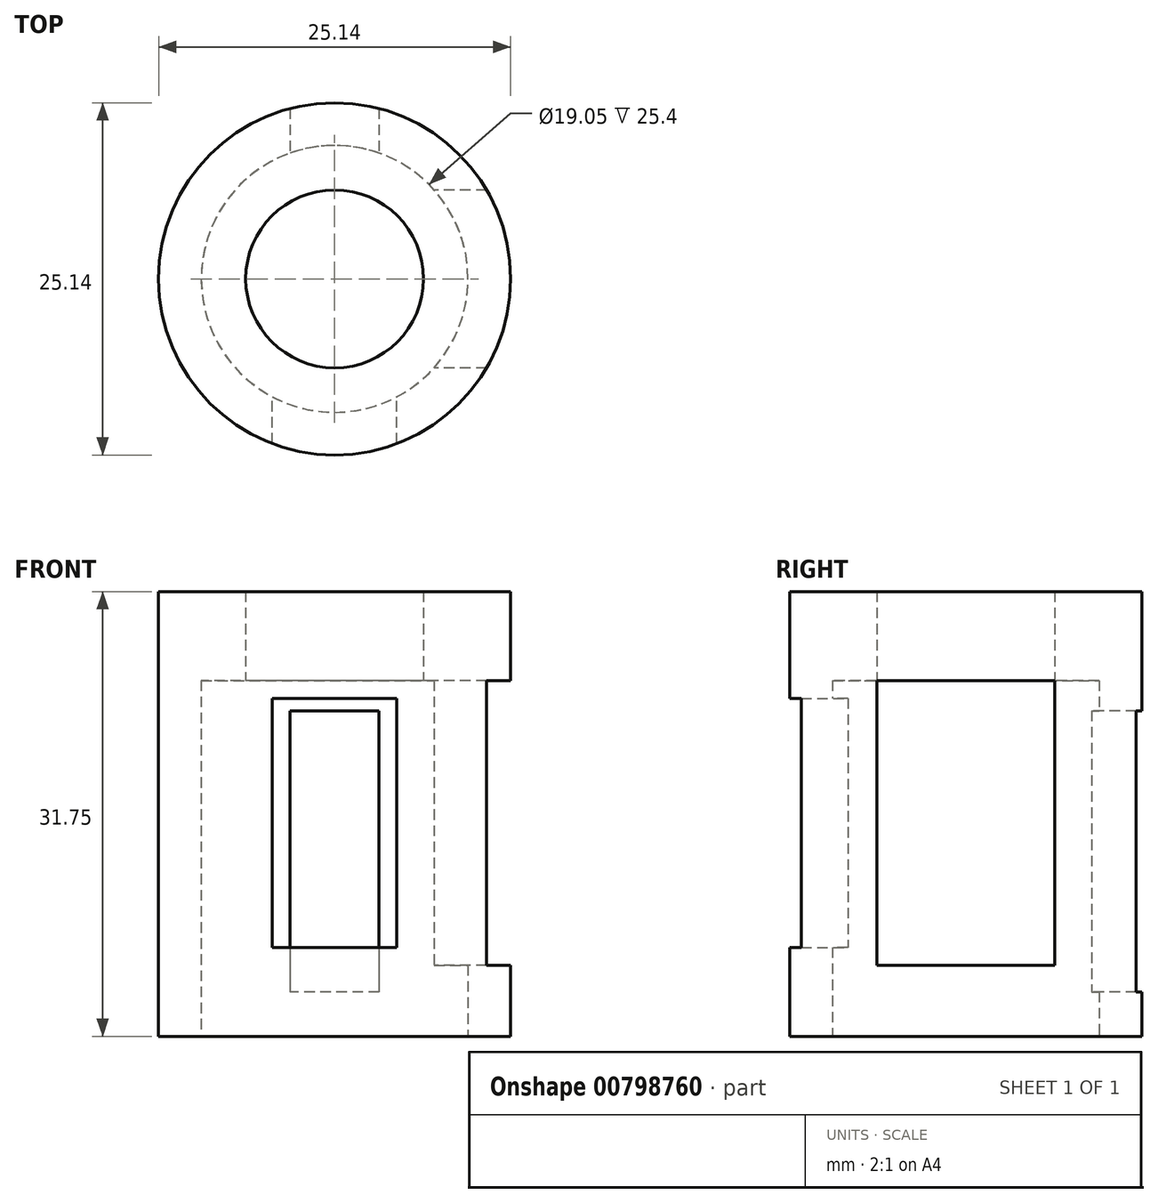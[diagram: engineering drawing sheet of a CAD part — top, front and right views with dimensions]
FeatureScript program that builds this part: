
annotation { "Feature Type Name" : "Feature", "Feature Type Description" : "" }
export const myFeature = defineFeature(function(context is Context, id is Id, definition is map)
    precondition{}
    {
        {
            var Q0;
            Q0=qCreatedBy(makeId("Top.planeOp"),FACE);
            var sketch = newSketch(context, id + "F0", { "sketchPlane" : qUnion([Q0])});
            skCircle(sketch, "E0", {"center": v(0, 0) * mm, "radius": 12.57 * mm});
            skSolve(sketch);
        }
        {
            var Q0;
            Q0=makeQuery(id+"F0.imprint","IMPRINT",FACE,{"disambiguationData":[TD([[makeQuery(id+"F0.imprint","IMPRINT",EDGE,{"derivedFrom":sQuery(id+"F0.wireOp",EDGE,"E0")}),1.0]])]});
            extrude(context, id + "F1", {"entities" : qUnion([Q0]), "depth" : 31.75 * mm, "offsetDistance" : 25.4 * mm});
        }
        {
            var Q0;
            Q0=qCreatedBy(makeId("Right.planeOp"),FACE);
            cPlane(context, id + "F2", {"entities" : qUnion([Q0]), "cplaneType" : CPlaneType.OFFSET, "offset" : 5.6 * mm, "width" : 152.4 * mm, "height" : 152.4 * mm});
        }
        {
            var Q0;
            Q0=qCreatedBy(id+"F2.planeOp",FACE);
            var sketch = newSketch(context, id + "F3", { "sketchPlane" : qUnion([Q0])});
            skLineSegment(sketch, "E1.bottom", {"start": v(-6.35, 25.4) * mm, "end": v(6.35, 25.4) * mm});
            skLineSegment(sketch, "E1.top", {"start": v(-6.35, 5.08) * mm, "end": v(6.35, 5.08) * mm});
            skLineSegment(sketch, "E1.left", {"start": v(-6.35, 25.4) * mm, "end": v(-6.35, 5.08) * mm});
            skLineSegment(sketch, "E1.right", {"start": v(6.35, 25.4) * mm, "end": v(6.35, 5.08) * mm});
            skSolve(sketch);
        }
        {
            var Q0;
            Q0 = qSketchRegion(id + "F3", true);
            extrude(context, id + "F4", {"entities" : qUnion([Q0]), "operationType" : NewBodyOperationType.REMOVE, "endBound" : BoundingType.THROUGH_ALL, "depth" : 25.4 * mm, "offsetDistance" : 25.4 * mm});
        }
        {
            var Q0;
            Q0=qCreatedBy(makeId("Front.planeOp"),FACE);
            cPlane(context, id + "F5", {"entities" : qUnion([Q0]), "cplaneType" : CPlaneType.OFFSET, "offset" : 2.41 * mm, "oppositeDirection" : true, "width" : 152.4 * mm, "height" : 152.4 * mm});
        }
        {
            var Q0;
            Q0=qCreatedBy(id+"F5.planeOp",FACE);
            var sketch = newSketch(context, id + "F6", { "sketchPlane" : qUnion([Q0])});
            skLineSegment(sketch, "E2.bottom", {"start": v(3.18, 23.24) * mm, "end": v(-3.18, 23.24) * mm});
            skLineSegment(sketch, "E2.top", {"start": v(3.17, 3.18) * mm, "end": v(-3.17, 3.18) * mm});
            skLineSegment(sketch, "E2.left", {"start": v(3.17, 23.24) * mm, "end": v(3.17, 3.18) * mm});
            skLineSegment(sketch, "E2.right", {"start": v(-3.18, 23.24) * mm, "end": v(-3.18, 3.18) * mm});
            skSolve(sketch);
        }
        {
            var Q0;
            Q0 = qSketchRegion(id + "F6", true);
            extrude(context, id + "F7", {"entities" : qUnion([Q0]), "operationType" : NewBodyOperationType.REMOVE, "endBound" : BoundingType.THROUGH_ALL, "oppositeDirection" : true, "depth" : 25.4 * mm, "offsetDistance" : 25.4 * mm});
        }
        {
            var Q0;
            Q0=qCreatedBy(makeId("Front.planeOp"),FACE);
            var sketch = newSketch(context, id + "F8", { "sketchPlane" : qUnion([Q0])});
            skLineSegment(sketch, "E3.bottom", {"start": v(-4.44, 24.13) * mm, "end": v(4.44, 24.13) * mm});
            skLineSegment(sketch, "E3.top", {"start": v(-4.44, 6.35) * mm, "end": v(4.44, 6.35) * mm});
            skLineSegment(sketch, "E3.left", {"start": v(-4.45, 24.13) * mm, "end": v(-4.45, 6.35) * mm});
            skLineSegment(sketch, "E3.right", {"start": v(4.45, 24.13) * mm, "end": v(4.45, 6.35) * mm});
            skSolve(sketch);
        }
        {
            var Q0;
            Q0 = qSketchRegion(id + "F8", true);
            extrude(context, id + "F9", {"entities" : qUnion([Q0]), "operationType" : NewBodyOperationType.REMOVE, "endBound" : BoundingType.THROUGH_ALL, "depth" : 25.4 * mm, "offsetDistance" : 25.4 * mm});
        }
        {
            var Q0;
            Q0=qCreatedBy(makeId("Top.planeOp"),FACE);
            var sketch = newSketch(context, id + "F10", { "sketchPlane" : qUnion([Q0])});
            skCircle(sketch, "E4", {"center": v(0, 0) * mm, "radius": 6.35 * mm});
            skSolve(sketch);
        }
        {
            var Q0;
            Q0 = qSketchRegion(id + "F10", true);
            extrude(context, id + "F11", {"entities" : qUnion([Q0]), "operationType" : NewBodyOperationType.REMOVE, "endBound" : BoundingType.THROUGH_ALL, "depth" : 25.4 * mm, "offsetDistance" : 25.4 * mm});
        }
        {
            var Q0;
            Q0=makeQuery(id+"F1.opExtrude","CAP_FACE",FACE,{"disambiguationData":[OSD([sQuery(id+"F0.wireOp",EDGE,"E0")])],"isStart":true});
            var sketch = newSketch(context, id + "F12", { "sketchPlane" : qUnion([Q0])});
            skCircle(sketch, "E5", {"center": v(0, 0) * mm, "radius": 9.53 * mm});
            skSolve(sketch);
        }
        {
            var Q0;
            Q0 = qSketchRegion(id + "F12", true);
            extrude(context, id + "F13", {"entities" : qUnion([Q0]), "operationType" : NewBodyOperationType.REMOVE, "oppositeDirection" : true, "depth" : 25.4 * mm, "offsetDistance" : 25.4 * mm});
        }
    });
